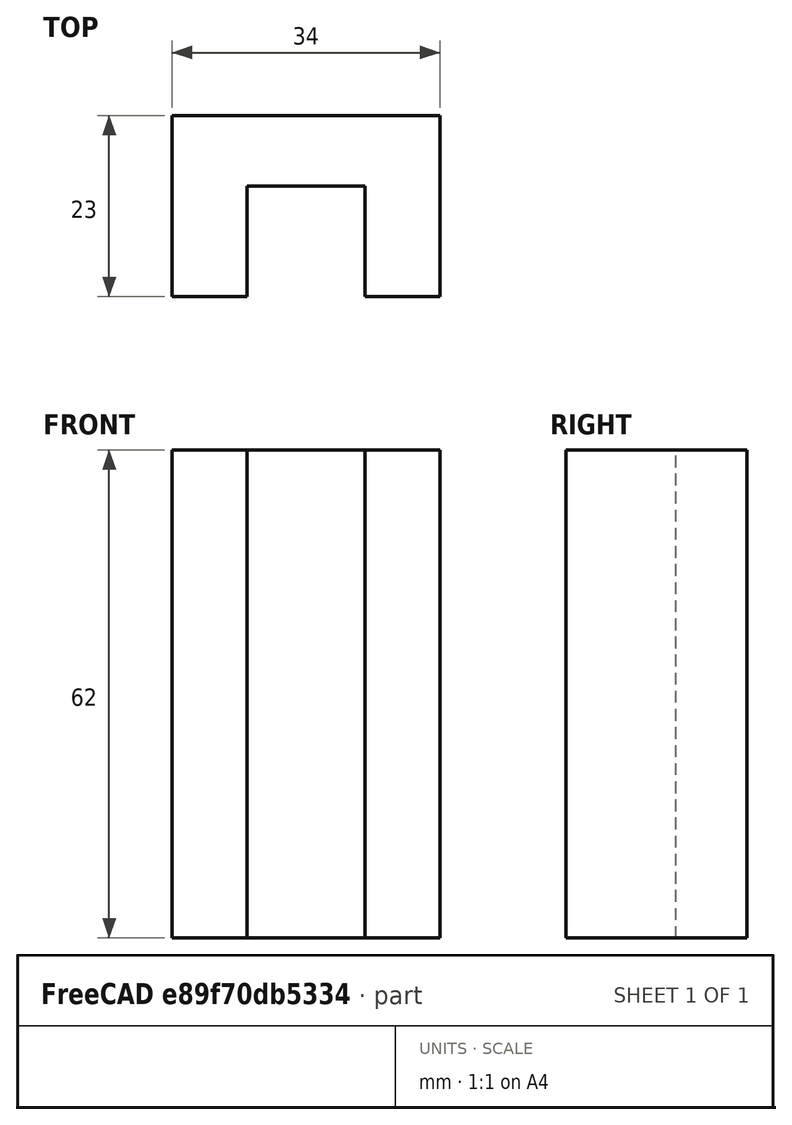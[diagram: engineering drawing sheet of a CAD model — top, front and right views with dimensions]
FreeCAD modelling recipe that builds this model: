
FCSTD DOCUMENT  (FreeCAD 0.21R33771 (Git))
Label: Pattino-15
License: All rights reserved
LicenseURL: http://en.wikipedia.org/wiki/All_rights_reserved
objects: Sketcher::SketchObject×2, PartDesign::Pad×1, PartDesign::CoordinateSystem×1, PartDesign::Body×1
note: 6 computed .brp shape members not serialized (recipe doc carries the construction recipe); baked Part::Feature solids carry a one-line shape summary decoded from their .brp

FEATURE [Sketcher::SketchObject] Sketch
  FullyConstrained = true
  MapMode = 5
  Support = -> [XY_Plane]
  sketch-geometry (8):
    g0: LineSegment StartX=0 StartY=0 StartZ=0 EndX=9.5 EndY=0 EndZ=0
    g1: LineSegment StartX=34 StartY=0 StartZ=0 EndX=34 EndY=23 EndZ=0
    g2: LineSegment StartX=34 StartY=23 StartZ=0 EndX=0 EndY=23 EndZ=0
    g3: LineSegment StartX=0 StartY=23 StartZ=0 EndX=0 EndY=0 EndZ=0
    g4: LineSegment StartX=9.5 StartY=0 StartZ=0 EndX=9.5 EndY=14 EndZ=0
    g5: LineSegment StartX=9.5 StartY=14 StartZ=0 EndX=24.5 EndY=14 EndZ=0
    g6: LineSegment StartX=24.5 StartY=14 StartZ=0 EndX=24.5 EndY=0 EndZ=0
    g7: LineSegment StartX=24.5 StartY=0 StartZ=0 EndX=34 EndY=0 EndZ=0
  constraints (22):
    c: Coincident(g7,g1)
    c: Coincident(g1,g2)
    c: Coincident(g2,g3)
    c: Coincident(g3,g0)
    c: Horizontal(g0)
    c: Horizontal(g2)
    c: Vertical(g1)
    c: Vertical(g3)
    c: Coincident(g0,g-1)
    c: DistanceY(g1,g1) = 23
    c: DistanceX(g2,g2) = 34
    c: Vertical(g4)
    c: Coincident(g5,g4)
    c: Horizontal(g5)
    c: Coincident(g6,g5)
    c: Vertical(g6)
    c: Coincident(g0,g4)
    c: Coincident(g7,g6)
    c: Tangent(g0,g7)
    c: DistanceX(g5,g5) = 15
    c: DistanceX(g0,g0) = 9.5
    c: DistanceY(g6,g6) = 14
FEATURE [PartDesign::Pad] Pad
  Direction = (0,0,1)
  Length = 62
  Length2 = 100
  Profile = -> Sketch
  ReferenceAxis = -> Sketch [N_Axis]
  Type = 0
FEATURE [Sketcher::SketchObject] Sketch002
  FullyConstrained = true
  MapMode = 5
  Placement = pos=(0,23,0) rot=(0,0.707107,0.707107;3.14159rad)
  Support = -> [Pad]
  sketch-geometry (8):
    g0: LineSegment StartX=-30 StartY=48 StartZ=0 EndX=-30 EndY=14 EndZ=0
    g1: LineSegment StartX=-30 StartY=14 StartZ=0 EndX=-4 EndY=14 EndZ=0
    g2: Circle CenterX=-30 CenterY=48 CenterZ=0 NormalX=0 NormalY=0 NormalZ=1 AngleXU=0 Radius=2.1
    g3: Circle CenterX=-30 CenterY=14 CenterZ=0 NormalX=0 NormalY=0 NormalZ=1 AngleXU=0 Radius=0
    g4: Circle CenterX=-4 CenterY=14 CenterZ=0 NormalX=0 NormalY=0 NormalZ=1 AngleXU=0 Radius=2.1
    g5: Circle CenterX=-4 CenterY=48 CenterZ=0 NormalX=0 NormalY=0 NormalZ=1 AngleXU=0 Radius=2.1
    g6: LineSegment StartX=-30 StartY=48 StartZ=0 EndX=-4 EndY=48 EndZ=0
    g7: Circle CenterX=-30 CenterY=14 CenterZ=0 NormalX=0 NormalY=0 NormalZ=1 AngleXU=0 Radius=2.1
  constraints (20):
    c: Vertical(g0)
    c: Coincident(g1,g0)
    c: Horizontal(g1)
    c: Coincident(g2,g0)
    c: Coincident(g3,g0)
    c: Tangent(g3,g1)
    c: Coincident(g4,g1)
    c: Coincident(g6,g0)
    c: Coincident(g6,g5)
    c: Coincident(g7,g0)
    c: Equal(g2,g7)
    c: Equal(g2,g5)
    c: Equal(g2,g4)
    c: Radius(g2) = 2.1
    c: Horizontal(g5,g0)
    c: DistanceY(g0,g0) = 34
    c: Equal(g6,g1)
    c: DistanceX(g1,g1) = 26
    c: DistanceX(g1,g-1) = 4
    c: DistanceY(g-1,g1) = 14
FEATURE [PartDesign::CoordinateSystem] LCS_Pattino1  label="LCS_Pattino15"
  AttacherType = Attacher::AttachEngine3D
FEATURE [PartDesign::Body] Body
  Group = -> [Sketch,Pad,Sketch002,LCS_Pattino1]
  Origin = -> Origin
  Tip = -> Pad
